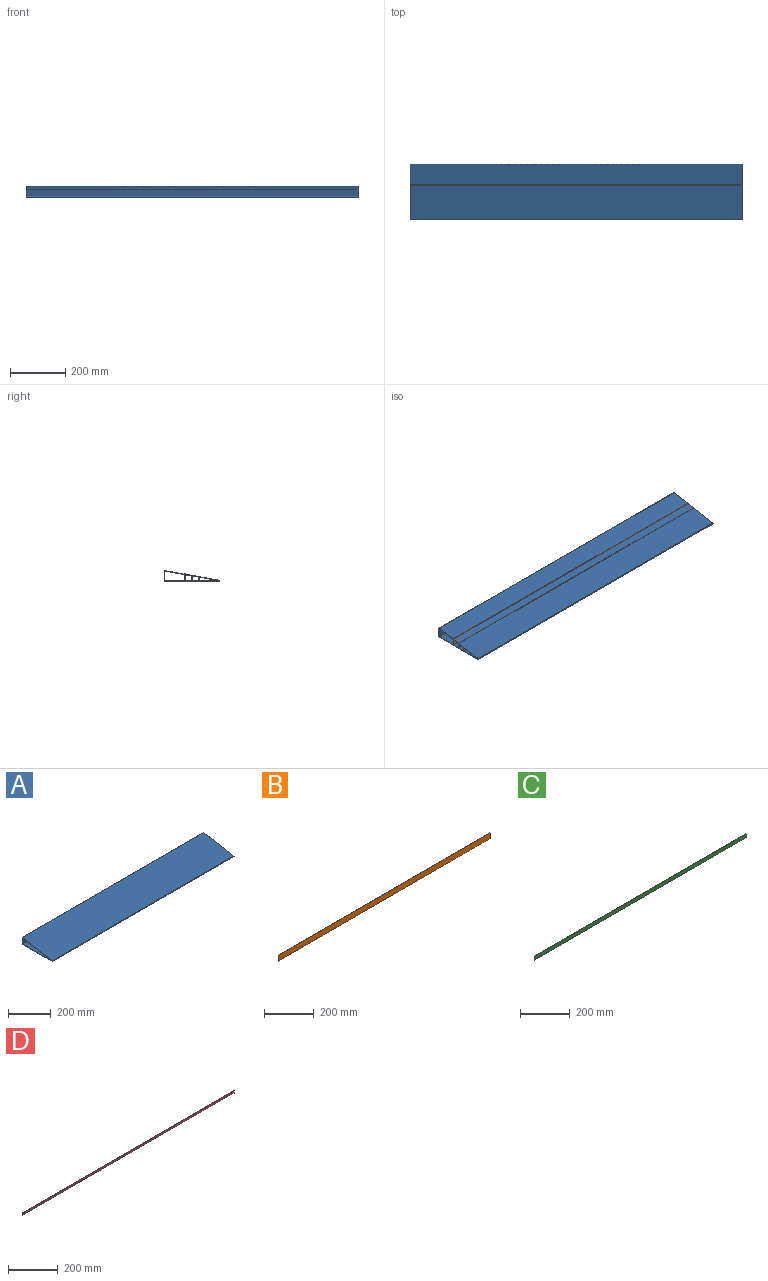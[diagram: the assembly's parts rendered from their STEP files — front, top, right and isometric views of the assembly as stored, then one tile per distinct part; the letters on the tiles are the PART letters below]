
ASSEMBLY  parts=4 mates=3
PART A: 24 faces, bbox 1200x202x40 mm
  f0: plane 35.56x2mm, normal (1,0,0), area 71.1mm2, adj f2,f3,f13,f21
  f1: plane 35.56x2mm, normal (-1,0,0), area 71.1mm2, adj f2,f3,f12,f20
  f2: plane 1200x35.56mm, normal (0,1,0), area 42672.9mm2, adj f0,f1,f14,f22
  f3: plane 1200x35.56mm, normal (0,-1,0), area 42672.9mm2, adj f0,f1,f15,f23
  f4: plane 197.56x2mm, normal (1,0,0), area 395.1mm2, adj f6,f7,f17,f21
  f5: plane 197.56x2mm, normal (-1,0,0), area 395.1mm2, adj f6,f7,f16,f20
  f6: plane 1200x197.56mm, normal (0,0,-1), area 237071.9mm2, adj f4,f5,f18,f22
  f7: plane 1200x197.56mm, normal (0,0,1), area 237071.9mm2, adj f4,f5,f19,f23
  f8: plane 197.91x37.53mm, normal (1,0,0), area 401.5mm2, adj f10,f11,f13,f17
  f9: plane 197.91x37.53mm, normal (-1,0,0), area 401.5mm2, adj f10,f11,f12,f16
  f10: plane 1200x197.56mm, normal (0,-0.18,0.98), area 240881.9mm2, adj f8,f9,f14,f18
  f11: plane 1200x197.56mm, normal (0,0.18,-0.98), area 240881.9mm2, adj f8,f9,f15,f19
  f12: plane 2.59x2.2mm, normal (-1,0,0), area 4.2mm2, adj f1,f9,f14,f15
  f13: plane 2.59x2.2mm, normal (1,0,0), area 4.2mm2, adj f0,f8,f14,f15
  f14: cylinder r=2.2mm len=1200mm, axis (-1,0,0), area 4617.1mm2, adj f2,f10,f12,f13
  f15: cylinder r=0.2mm len=1200mm, axis (-1,0,0), area 419.7mm2, adj f3,f11,f12,f13
  f16: plane 4.37x2.2mm, normal (-1,0,0), area 7.1mm2, adj f5,f9,f18,f19
  f17: plane 4.37x2.2mm, normal (1,0,0), area 7.1mm2, adj f4,f8,f18,f19
  f18: cylinder r=2.2mm len=1200mm, axis (-1,0,0), area 7823.6mm2, adj f6,f10,f16,f17
  f19: cylinder r=0.2mm len=1200mm, axis (-1,0,0), area 711.2mm2, adj f7,f11,f16,f17
  f20: plane 2.2x2.2mm, normal (-1,0,0), area 3.8mm2, adj f1,f5,f22,f23
  f21: plane 2.2x2.2mm, normal (1,0,0), area 3.8mm2, adj f0,f4,f22,f23
  f22: cylinder r=2.2mm len=1200mm, axis (-1,0,0), area 4146.9mm2, adj f2,f6,f20,f21
  f23: cylinder r=0.2mm len=1200mm, axis (-1,0,0), area 377mm2, adj f3,f7,f20,f21
PART B: 6 faces, bbox 1200x2x28 mm
  f0: plane 1200x2mm, normal (0,0,-1), area 2400mm2, adj f1,f3,f4,f5
  f1: plane 28x2mm, normal (1,0,0), area 56mm2, adj f0,f2,f4,f5
  f2: plane 1200x2mm, normal (0,0,1), area 2400mm2, adj f1,f3,f4,f5
  f3: plane 28x2mm, normal (-1,0,0), area 56mm2, adj f0,f2,f4,f5
  f4: plane 1200x28mm, normal (0,-1,0), area 33600mm2, adj f0,f1,f2,f3
  f5: plane 1200x28mm, normal (0,1,0), area 33600mm2, adj f0,f1,f2,f3
PART C: 6 faces, bbox 1200x2x19 mm
  f0: plane 1200x2mm, normal (0,0,-1), area 2400mm2, adj f1,f3,f4,f5
  f1: plane 19x2mm, normal (1,0,0), area 38mm2, adj f0,f2,f4,f5
  f2: plane 1200x2mm, normal (0,0,1), area 2400mm2, adj f1,f3,f4,f5
  f3: plane 19x2mm, normal (-1,0,0), area 38mm2, adj f0,f2,f4,f5
  f4: plane 1200x19mm, normal (0,-1,0), area 22800mm2, adj f0,f1,f2,f3
  f5: plane 1200x19mm, normal (0,1,0), area 22800mm2, adj f0,f1,f2,f3
PART D: 6 faces, bbox 1200x2x10 mm
  f0: plane 1200x2mm, normal (0,0,-1), area 2400mm2, adj f1,f3,f4,f5
  f1: plane 10x2mm, normal (1,0,0), area 20mm2, adj f0,f2,f4,f5
  f2: plane 1200x2mm, normal (0,0,1), area 2400mm2, adj f1,f3,f4,f5
  f3: plane 10x2mm, normal (-1,0,0), area 20mm2, adj f0,f2,f4,f5
  f4: plane 1200x10mm, normal (0,-1,0), area 12000mm2, adj f0,f1,f2,f3
  f5: plane 1200x10mm, normal (0,1,0), area 12000mm2, adj f0,f1,f2,f3
PLACE A t=(-107.17,37.08,67.18)mm
PLACE B t=(1092.83,-35.9,67.18)mm
PLACE C t=(1092.83,-60.9,67.18)mm
PLACE D t=(1092.83,-85.9,67.18)mm
MATE fastened B.f0 <-> A.f7  axis (0,0,-1) through (-107.17,-36.9,67.18)mm
MATE fastened C.f0 <-> A.f7  axis (0,0,-1) through (1092.83,-61.9,67.18)mm
MATE fastened D.f0 <-> A.f7  axis (0,0,-1) through (1092.83,-86.9,67.18)mm
